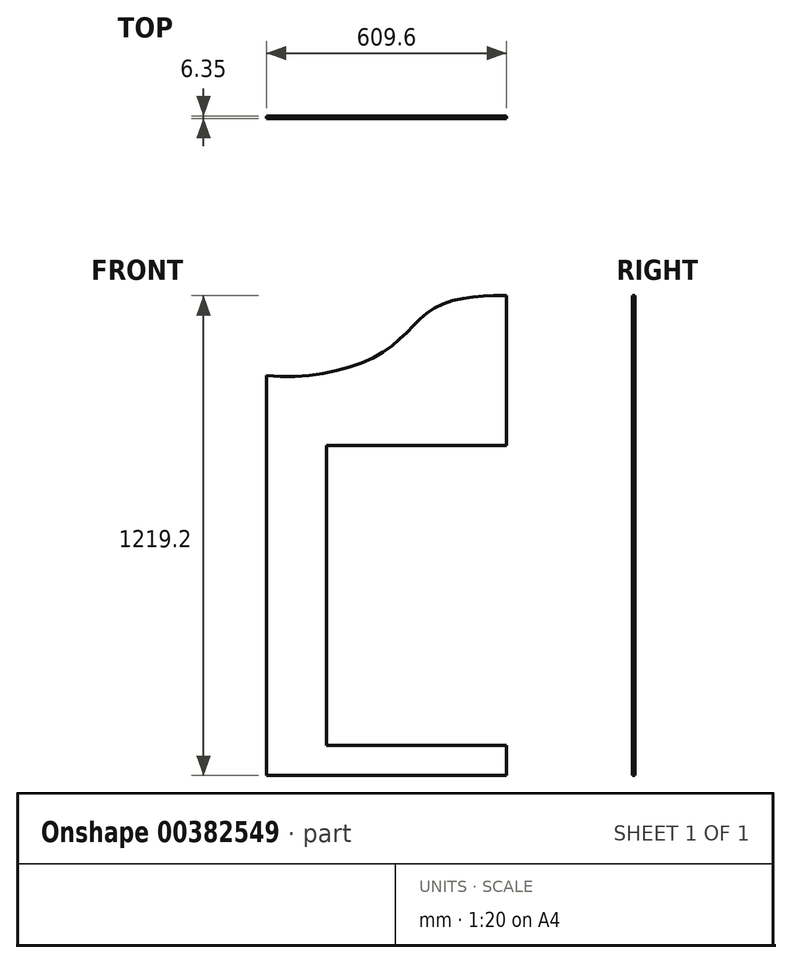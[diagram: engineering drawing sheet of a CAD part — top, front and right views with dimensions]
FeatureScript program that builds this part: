
annotation { "Feature Type Name" : "Feature", "Feature Type Description" : "" }
export const myFeature = defineFeature(function(context is Context, id is Id, definition is map)
    precondition{}
    {
        {
            var Q0;
            Q0=qCreatedBy(makeId("Front.planeOp"),FACE);
            var sketch = newSketch(context, id + "F0", { "sketchPlane" : qUnion([Q0])});
            skLineSegment(sketch, "E0.bottom", {"start": v(304.8, 609.6) * mm, "end": v(-304.8, 609.6) * mm});
            skLineSegment(sketch, "E0.top", {"start": v(304.8, -609.6) * mm, "end": v(-304.8, -609.6) * mm});
            skLineSegment(sketch, "E0.left", {"start": v(304.8, 609.6) * mm, "end": v(304.8, -609.6) * mm});
            skLineSegment(sketch, "E0.right", {"start": v(-304.8, 609.6) * mm, "end": v(-304.8, -609.6) * mm});
            skPoint(sketch, "E0.middle", {"position": v(0, 0) * mm});
            skSolve(sketch);
        }
        {
            var Q0;
            Q0=makeQuery(id+"F0.imprint","IMPRINT",FACE,{"disambiguationData":[TD([[makeQuery(id+"F0.imprint","IMPRINT",EDGE,{"derivedFrom":sQuery(id+"F0.wireOp",EDGE,"E0.bottom")}),1.0]])]});
            extrude(context, id + "F1", {"entities" : qUnion([Q0]), "depth" : 6.35 * mm});
        }
        {
            var Q0;
            Q0=makeQuery(id+"F1.opExtrude","CAP_FACE",FACE,{"disambiguationData":[OSD([sQuery(id+"F0.wireOp",EDGE,"E0.bottom"),sQuery(id+"F0.wireOp",EDGE,"E0.top"),sQuery(id+"F0.wireOp",EDGE,"E0.left"),sQuery(id+"F0.wireOp",EDGE,"E0.right")])],"isStart":false});
            var sketch = newSketch(context, id + "F2", { "sketchPlane" : qUnion([Q0])});
            skLineSegment(sketch, "E1.bottom", {"start": v(304.8, 228.6) * mm, "end": v(-152.4, 228.6) * mm});
            skLineSegment(sketch, "E1.top", {"start": v(304.8, -533.4) * mm, "end": v(-152.4, -533.4) * mm});
            skLineSegment(sketch, "E1.left", {"start": v(304.8, 228.6) * mm, "end": v(304.8, -533.4) * mm});
            skLineSegment(sketch, "E1.right", {"start": v(-152.4, 228.6) * mm, "end": v(-152.4, -533.4) * mm});
            skSolve(sketch);
        }
        {
            var Q0;
            Q0=makeQuery(id+"F2.imprint","IMPRINT",FACE,{"disambiguationData":[TD([[makeQuery(id+"F2.imprint","IMPRINT",EDGE,{"derivedFrom":sQuery(id+"F2.wireOp",EDGE,"E1.bottom")}),1.0]])]});
            extrude(context, id + "F3", {"entities" : qUnion([Q0]), "operationType" : NewBodyOperationType.REMOVE, "endBound" : BoundingType.THROUGH_ALL, "oppositeDirection" : true, "depth" : 25.4 * mm});
        }
        {
            var Q0;
            Q0=makeQuery(id+"F1.opExtrude","CAP_FACE",FACE,{"disambiguationData":[OSD([sQuery(id+"F0.wireOp",EDGE,"E0.bottom"),sQuery(id+"F0.wireOp",EDGE,"E0.top"),sQuery(id+"F0.wireOp",EDGE,"E0.left"),sQuery(id+"F0.wireOp",EDGE,"E0.right")])],"isStart":false});
            var sketch = newSketch(context, id + "F4", { "sketchPlane" : qUnion([Q0])});
            skFitSpline(sketch, "E2", {"points": [v(304.8, 609.6) * mm, v(127.4, 581.4) * mm, v(0, 471.76) * mm, v(-304.8, 406.4) * mm], "startDerivative": vector(-520.26, 1.3) * mm, "endDerivative": vector(-836.3, 80.32) * mm});
            skLineSegment(sketch, "E3", {"start": v(-304.8, 406.4) * mm, "end": v(-304.8, 609.6) * mm});
            skLineSegment(sketch, "E4", {"start": v(-304.8, 609.6) * mm, "end": v(304.8, 609.6) * mm});
            skSolve(sketch);
        }
        {
            var Q0;
            {var subQ0=sQuery(id+"F4.wireOp",EDGE,"E3");Q0=makeQuery(id+"F4.imprint","IMPRINT",FACE,{"disambiguationData":[TD([[makeQuery(id+"F4.imprint","IMPRINT",EDGE,{"derivedFrom":subQ0}),1.0]])]});}
            extrude(context, id + "F5", {"entities" : qUnion([Q0]), "operationType" : NewBodyOperationType.REMOVE, "endBound" : BoundingType.THROUGH_ALL, "oppositeDirection" : true, "depth" : 25.4 * mm});
        }
    });
